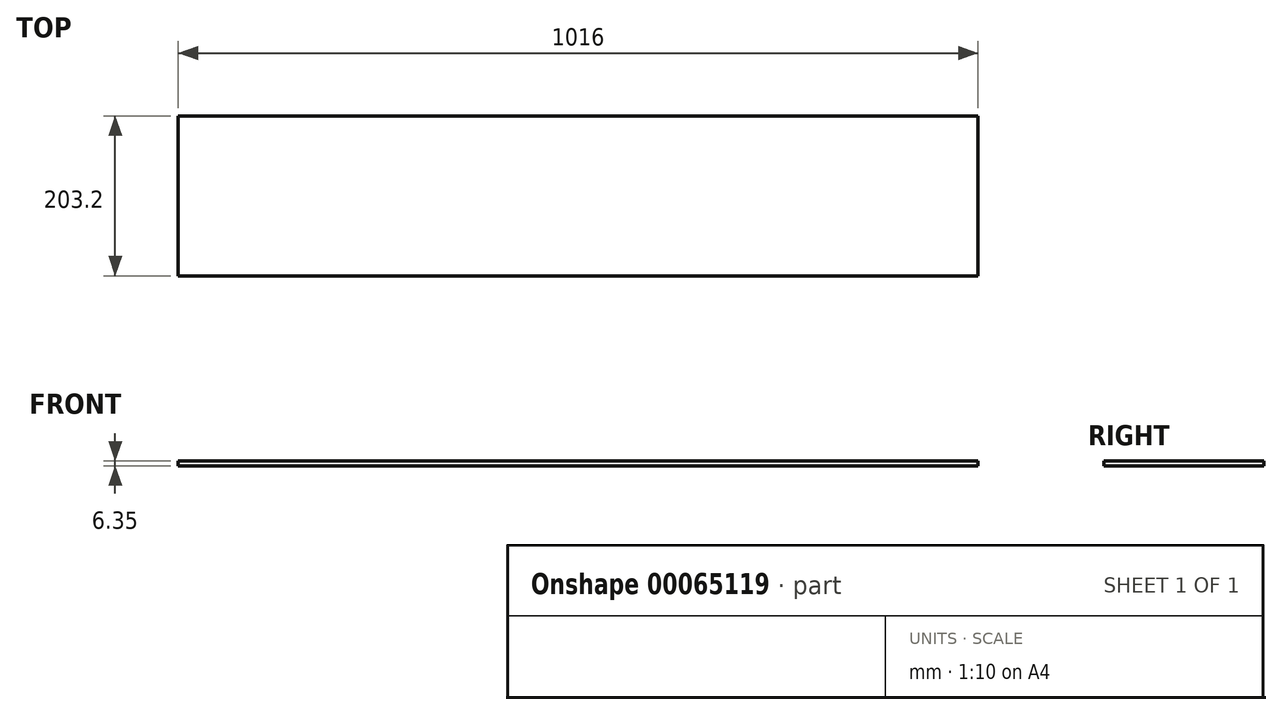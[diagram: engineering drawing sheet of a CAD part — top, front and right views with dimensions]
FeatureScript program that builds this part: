
annotation { "Feature Type Name" : "Feature", "Feature Type Description" : "" }
export const myFeature = defineFeature(function(context is Context, id is Id, definition is map)
    precondition{}
    {
        {
            var Q0;
            Q0=qCreatedBy(makeId("Top.planeOp"),FACE);
            var sketch = newSketch(context, id + "F0", { "sketchPlane" : qUnion([Q0])});
            skLineSegment(sketch, "E0.rect.bottom", {"start": v(508, 101.6) * mm, "end": v(-508, 101.6) * mm});
            skLineSegment(sketch, "E0.rect.top", {"start": v(508, -101.6) * mm, "end": v(-508, -101.6) * mm});
            skLineSegment(sketch, "E0.rect.left", {"start": v(508, 101.6) * mm, "end": v(508, -101.6) * mm});
            skLineSegment(sketch, "E0.rect.right", {"start": v(-508, 101.6) * mm, "end": v(-508, -101.6) * mm});
            skPoint(sketch, "E0.rect.middle", {"position": v(0, 0) * mm});
            skSolve(sketch);
        }
        {
            var Q0;
            Q0 = qSketchRegion(id + "F0", true);
            extrude(context, id + "F1", {"entities" : qUnion([Q0]), "depth" : 6.35 * mm});
        }
    });
